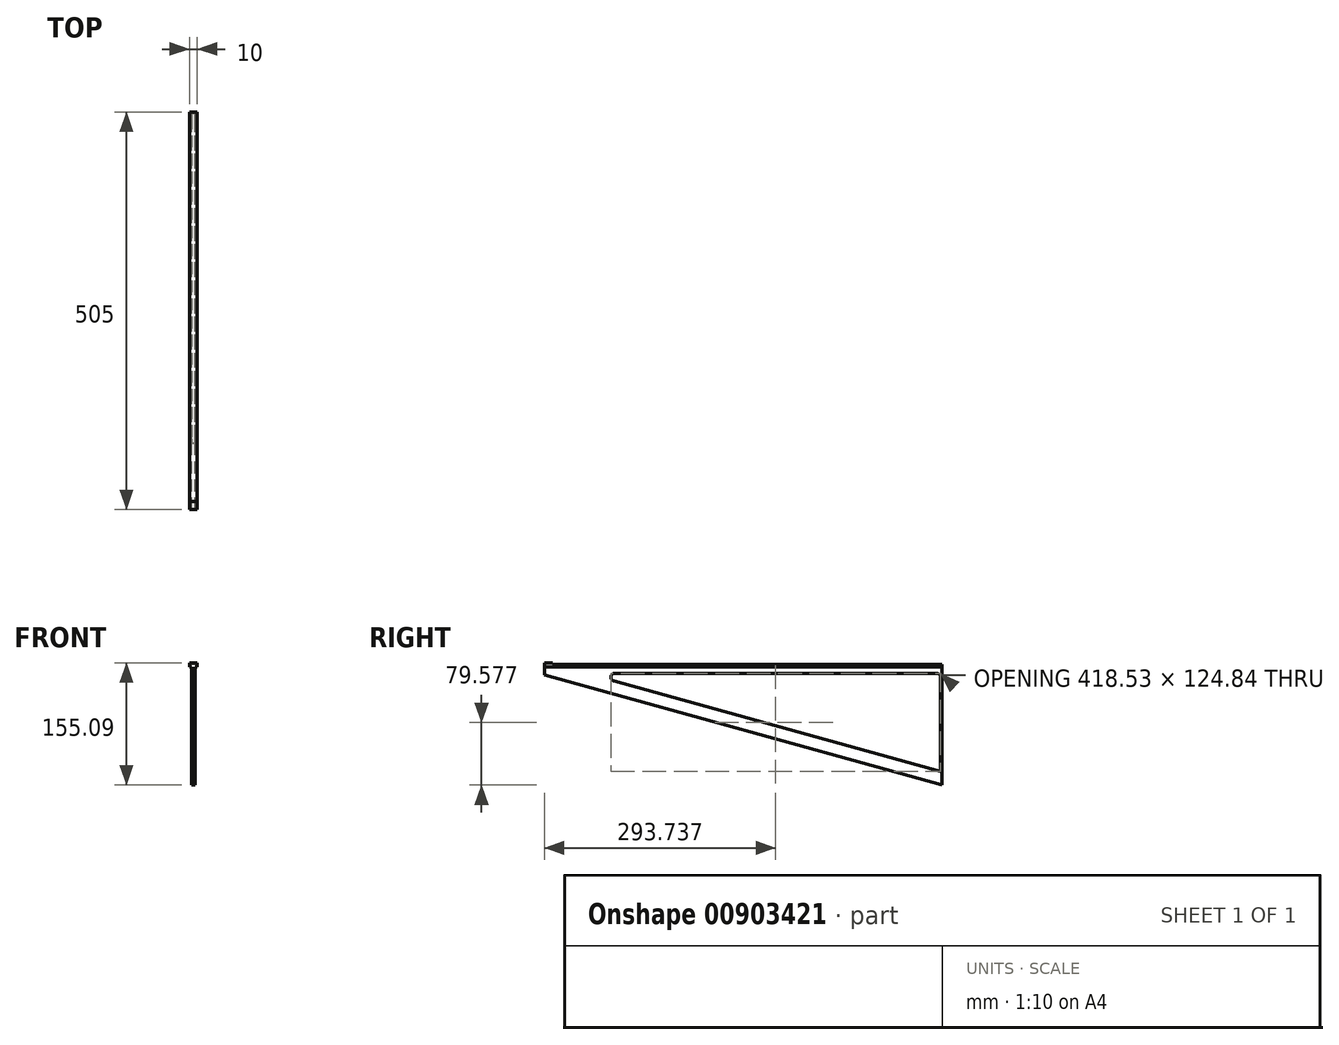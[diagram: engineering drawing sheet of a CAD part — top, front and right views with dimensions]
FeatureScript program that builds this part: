
annotation { "Feature Type Name" : "Feature", "Feature Type Description" : "" }
export const myFeature = defineFeature(function(context is Context, id is Id, definition is map)
    precondition{}
    {
        {
            var Q0;
            Q0=qCreatedBy(makeId("Front.planeOp"),FACE);
            var sketch = newSketch(context, id + "F0", { "sketchPlane" : qUnion([Q0])});
            skLineSegment(sketch, "E0", {"start": v(-7, 5.96) * mm, "end": v(-7, 2.87) * mm});
            skLineSegment(sketch, "E1", {"start": v(-7, 2.87) * mm, "end": v(-4, 2.87) * mm});
            skLineSegment(sketch, "E2", {"start": v(-4, 2.87) * mm, "end": v(-4, -147.13) * mm});
            skLineSegment(sketch, "E3", {"start": v(-4, -147.13) * mm, "end": v(0, -147.13) * mm});
            skLineSegment(sketch, "E4", {"start": v(0, -147.13) * mm, "end": v(0, 2.87) * mm});
            skLineSegment(sketch, "E5", {"start": v(0, 2.87) * mm, "end": v(3, 2.87) * mm});
            skLineSegment(sketch, "E6", {"start": v(3, 2.87) * mm, "end": v(3, 5.96) * mm});
            skLineSegment(sketch, "E7", {"start": v(3, 5.96) * mm, "end": v(-7, 5.96) * mm});
            skSolve(sketch);
        }
        {
            var Q0;
            Q0 = qSketchRegion(id + "F0", true);
            extrude(context, id + "F1", {"entities" : qUnion([Q0]), "depth" : 505 * mm, "offsetDistance" : 25 * mm});
        }
        {
            var Q0;
            Q0=makeQuery(id+"F1.opExtrude","SWEPT_FACE",FACE,{"disambiguationData":[OSD([sQuery(id+"F0.wireOp",EDGE,"E7")])]});
            var sketch = newSketch(context, id + "F2", { "sketchPlane" : qUnion([Q0])});
            skLineSegment(sketch, "E8", {"start": v(-7, -505) * mm, "end": v(3, -505) * mm});
            skLineSegment(sketch, "E9", {"start": v(3, -505) * mm, "end": v(3, -495) * mm});
            skLineSegment(sketch, "E10", {"start": v(3, -495) * mm, "end": v(-7, -495) * mm});
            skLineSegment(sketch, "E11", {"start": v(-7, -495) * mm, "end": v(-7, -505) * mm});
            skSolve(sketch);
        }
        {
            var Q0;
            Q0 = qSketchRegion(id + "F2", true);
            extrude(context, id + "F3", {"entities" : qUnion([Q0]), "operationType" : NewBodyOperationType.ADD, "depth" : 2 * mm, "offsetDistance" : 25 * mm});
        }
        {
            var Q0;
            Q0=makeQuery(id+"F1.opExtrude","SWEPT_FACE",FACE,{"disambiguationData":[OSD([sQuery(id+"F0.wireOp",EDGE,"E2")])]});
            var sketch = newSketch(context, id + "F4", { "sketchPlane" : qUnion([Q0])});
            skLineSegment(sketch, "E12", {"start": v(505, -7.13) * mm, "end": v(0, -147.13) * mm});
            skSolve(sketch);
        }
        {
            var Q0;
            {var subQ0=sQuery(id+"F4.wireOp",EDGE,"E12");Q0=makeQuery(id+"F4.imprint","IMPRINT",FACE,{"disambiguationData":[TD([[makeQuery(id+"F4.imprint","IMPRINT",EDGE,{"derivedFrom":subQ0}),1.0]])]});}
            extrude(context, id + "F5", {"entities" : qUnion([Q0]), "operationType" : NewBodyOperationType.REMOVE, "oppositeDirection" : true, "depth" : 25 * mm, "offsetDistance" : 25 * mm});
        }
        {
            var Q0;
            Q0=makeQuery(id+"F1.opExtrude","SWEPT_FACE",FACE,{"disambiguationData":[OSD([sQuery(id+"F0.wireOp",EDGE,"E2")])]});
            var sketch = newSketch(context, id + "F6", { "sketchPlane" : qUnion([Q0])});
            skLineSegment(sketch, "E13", {"start": v(2, -5.13) * mm, "end": v(452.32, -5.13) * mm});
            skLineSegment(sketch, "E14", {"start": v(452.32, -5.13) * mm, "end": v(2, -129.97) * mm});
            skLineSegment(sketch, "E15", {"start": v(2, -129.97) * mm, "end": v(2, -5.13) * mm});
            skSolve(sketch);
        }
        {
            var Q0;
            Q0 = qSketchRegion(id + "F6", true);
            extrude(context, id + "F7", {"entities" : qUnion([Q0]), "operationType" : NewBodyOperationType.REMOVE, "oppositeDirection" : true, "depth" : 25 * mm, "offsetDistance" : 25 * mm});
        }
        {
            var Q0;
            Q0=makeQuery(id+"F7.boolean.opBoolean","COPY",EDGE,{"derivedFrom":makeQuery(id+"F7.opExtrude","SWEPT_EDGE",EDGE,{"disambiguationData":[OSD([sQuery(id+"F6.wireOp",EDGE,"WY4LouiN-QIns-9mVj-PR68-0INmVUmdUtyd"),sQuery(id+"F6.wireOp",EDGE,"E13")])]})});
            var Q1;
            Q1=makeQuery(id+"F7.boolean.opBoolean","COPY",EDGE,{"derivedFrom":makeQuery(id+"F7.opExtrude","SWEPT_EDGE",EDGE,{"disambiguationData":[OSD([sQuery(id+"F6.wireOp",EDGE,"WY4LouiN-QIns-9mVj-PR68-0INmVUmdUtyd"),sQuery(id+"F6.wireOp",EDGE,"8ongm2l5-RV8W-QnmL-g9XP-3kgsotIlQBA6")])]})});
            var Q2;
            Q2=makeQuery(id+"F7.boolean.opBoolean","COPY",EDGE,{"derivedFrom":makeQuery(id+"F7.opExtrude","SWEPT_EDGE",EDGE,{"disambiguationData":[OSD([sQuery(id+"F6.wireOp",EDGE,"E13"),sQuery(id+"F6.wireOp",EDGE,"8ongm2l5-RV8W-QnmL-g9XP-3kgsotIlQBA6")])]})});
            fillet(context, id + "F8", {"entities" : qUnion([Q0, Q1, Q2]), "radius" : 5 * mm, "tangentPropagation" : true, "allowEdgeOverflow" : false});
        }
    });
